# Revit family: Hager-VOLTA-Surface_mounted-IP30-With_Cover-With_DIN-Hosted-CH-fr
name_source: partatom
category: Electrical Equipment
units: mm (PartAtom-declared; Revit-internal decimal feet)

## family parameters
Cut with Voids When Loaded = No
Host = Face
Maintain Annotation Orientation = Yes
Panel Configuration = Two Columns, Circuits Across
Part Type = Panelboard
Room Calculation Point = No
Round Connector Dimension = Use Diameter
Shared = No

## types (10) — shared parameters
BC_MODEL_ID = 1547132
BC_OBJECT_ID = 513471
BC_OBJECT_VERSION = #9
Code hager = ADD-EC000214_EU
EF000003 - mode de montage = apparent
EF000008 - largeur = 305 mm  [stored 1.00066 ft]
EF000024 - résiste aux UV = No
EF000049 - profondeur = 96 mm  [stored 0.314961 ft]
EF000116 - numéro RAL = 9010
EF001062 - version CEM = No
EF001134 - rail DIN = Yes
EF002950 - nombre d'unités modulaires = 12
EF005474 - indice de protection (IP) = IP30
EF006244 - couvercle/porte transparente = No
EF006306 - avec serrure = No
EF015777 - borne à conducteur neutre = No
ETIM class code = EC000214
ETIM class name = Small distribution board
HG000001-nombre de colonnes = 1
HG000002-avec porte = Yes
HG000003-Gamme = VOLTA
HG000005-Epaisseur = 2 mm  [stored 0.00656168 ft]
HG000006-Encastré = No
HG000009-Porte à double battant = No
HG000010-Portes asymétriques = No
HG000012-Angle de pivotement de la porte = 90.00°
HG000013-Porte à gauche = No
HG000014-Porte à droite = Yes
HG000015-Visibilité de l'emprise de la porte = Yes
HG000016-Visibilité de la porte 3D = Yes
HG000017-Distance entre pôles = 18 mm  [stored 0.0590551 ft]
HG000060-RAL-number = 9010
HG000099-ID modèle Onfly = 507532
HGEF0002950-largeur en nombre de modules = 12
Manufacturer = Hager
Name = VOLTA-Surface_mounted-IP30-With_Cover-With_DIN-CH
Name BIM&CO = Electricity
Name hager = ADD_Enclosures_EC000214
Uniformat = Low Tension Service & Dist.
Uniformat code = D501001
zero-valued in all types: Default Elevation, EF000218 - profondeur de montage, EF000846 - largeur d'encastrement, EF001131 - profondeur interne, HG000007-Nombre de colonnes vides

## per-type parameters (varying)
| type | BC_VARIANT_ID | EF000007 - couleur | EF000040 - hauteur | EF000118 - avec plaque de montage | EF000266 - nombre de rangées | EF000332 - hauteur d'installation | EF001088 - possibilité de montage adossé | EF004462 - type de fermeture | EF009212 - type de couvercle | EF015776 - borne de mise à la terre | EF015941 - porte de transmission du signal | HG000004-Référence fabricant | HG000008-Nombre de rangées vides | HG000011-Rangées du bas vides | HGEF000266-Nombre de rangées |
| VOLTA-Surface_mounted_W305_H245_D96_12_Modular_Spacing-VA12A | 1174202 |  | 245 mm  [stored 0.803806 ft] | No | 1 | 0 mm  [stored 0 ft] | No |  |  | No | No | VA12A | 0 | No | 1 |
| VOLTA-Surface_mounted_W305_H370_D96_12_Modular_Spacing-VA24A | 1174203 | blanc | 370 mm  [stored 1.21391 ft] | No | 2 | 0 mm  [stored 0 ft] | Yes | autre | avec découpe | Yes | No | VA24A | 0 | No | 2 |
| VOLTA-Surface_mounted_W305_H515_D96_12_Modular_Spacing-VA36A | 1174204 | blanc | 515 mm  [stored 1.68963 ft] | No | 3 | 0 mm  [stored 0 ft] | Yes | autre | avec découpe | Yes | No | VA36A | 0 | No | 3 |
| VOLTA-Surface_mounted_W305_H515_D96_12_Modular_Spacing-VA36RM | 1174207 | blanc | 515 mm  [stored 1.68963 ft] | No | 3 | 0 mm  [stored 0 ft] | Yes | autre | avec découpe | No | No | VA36RM | 0 | No | 3 |
| VOLTA-Surface_mounted_W305_H640_D96_12_Modular_Spacing-VA48A | 1174211 | blanc | 640 mm  [stored 2.09974 ft] | No | 4 | 0 mm  [stored 0 ft] | Yes | autre | avec découpe | Yes | No | VA48A | 0 | No | 4 |
| VOLTA-Surface_mounted_W305_H765_D96_12_Modular_Spacing-VA602NWS | 1174212 | blanc | 765 mm  [stored 2.50984 ft] | Yes | 5 | 765 mm  [stored 2.50984 ft] | Yes | autre | avec découpe | Yes | No | VA602NWS | 3 | Yes | 5 |
| VOLTA-Surface_mounted_W305_H765_D96_12_Modular_Spacing-VA602WWS | 1174213 | blanc | 765 mm  [stored 2.50984 ft] | Yes | 5 | 765 mm  [stored 2.50984 ft] | Yes | autre | avec découpe | Yes | Yes | VA602WWS | 3 | Yes | 5 |
| VOLTA-Surface_mounted_W305_H765_D96_12_Modular_Spacing-VA603NWS | 1174214 | blanc | 765 mm  [stored 2.50984 ft] | Yes | 5 | 765 mm  [stored 2.50984 ft] | Yes | autre | avec découpe | Yes | No | VA603NWS | 2 | Yes | 5 |
| VOLTA-Surface_mounted_W305_H765_D96_12_Modular_Spacing-VA603WWS | 1174215 | blanc | 765 mm  [stored 2.50984 ft] | Yes | 5 | 765 mm  [stored 2.50984 ft] | Yes | autre | avec découpe | Yes | Yes | VA603WWS | 2 | Yes | 5 |
| VOLTA-Surface_mounted_W305_H765_D96_12_Modular_Spacing-VA60A | 1174216 | blanc | 765 mm  [stored 2.50984 ft] | No | 5 | 0 mm  [stored 0 ft] | Yes | autre | avec découpe | Yes | No | VA60A | 0 | No | 5 |

note: column(s) folded — value = type name in every type: Reference

note: [stored X ft] marks values corroborated as IEEE doubles in the binary element streams (Revit-internal decimal feet)

## geometry (parser evidence)
native form markers: Sweep x15
no freeform markers — native parametric forms only
